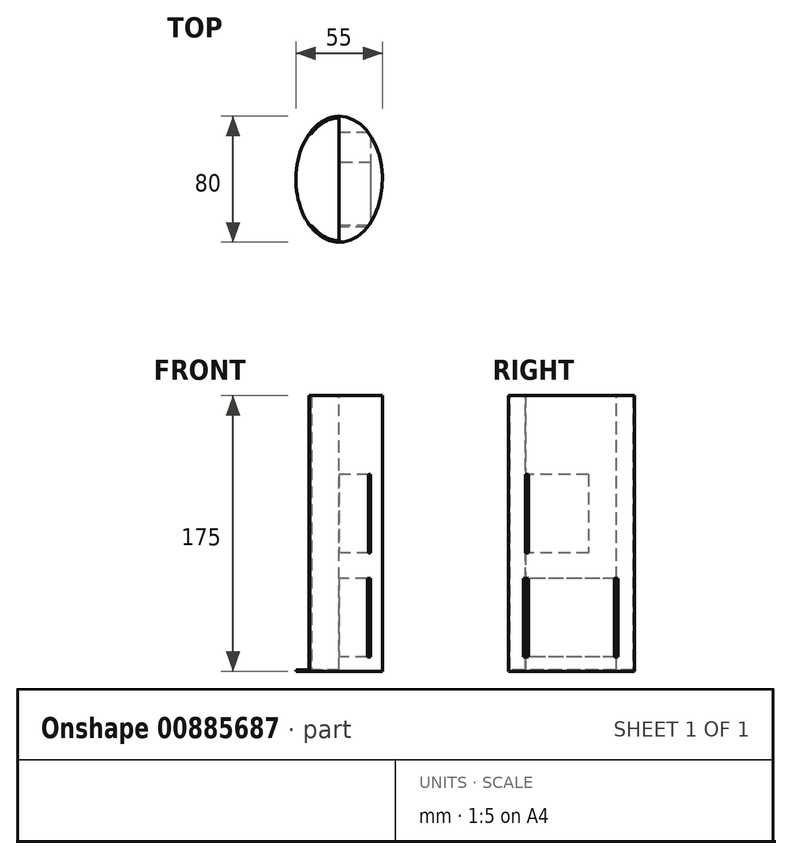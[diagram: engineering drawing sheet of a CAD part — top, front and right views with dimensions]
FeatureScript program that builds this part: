
annotation { "Feature Type Name" : "Feature", "Feature Type Description" : "" }
export const myFeature = defineFeature(function(context is Context, id is Id, definition is map)
    precondition{}
    {
        {
            var Q0;
            Q0=qCreatedBy(makeId("Top.planeOp"),FACE);
            var sketch = newSketch(context, id + "F0", { "sketchPlane" : qUnion([Q0])});
            skEllipse(sketch, "E0", {"center": v(-46.65, 29.27) * mm, "majorRadius": 27.5 * mm, "minorRadius": 40 * mm, "majorAxis": v(1, 0)});
            skSolve(sketch);
        }
        {
            var Q0;
            Q0 = qSketchRegion(id + "F0", true);
            extrude(context, id + "F1", {"entities" : qUnion([Q0]), "depth" : 175 * mm, "offsetDistance" : 25 * mm});
        }
        {
            var Q0;
            Q0=makeQuery(id+"F1.opExtrude","CAP_FACE",FACE,{"disambiguationData":[OSD([sQuery(id+"F0.wireOp",EDGE,"E0")])],"isStart":false});
            shell(context, id + "F2", {"entities" : qUnion([Q0]), "thickness" : 1 * mm});
        }
        {
            var Q0;
            Q0=makeQuery(id+"F1.opExtrude","CAP_FACE",FACE,{"disambiguationData":[OSD([sQuery(id+"F0.wireOp",EDGE,"E0")])],"isStart":false});
            var sketch = newSketch(context, id + "F3", { "sketchPlane" : qUnion([Q0])});
            skLineSegment(sketch, "E1.bottom", {"start": v(-60.73, 57.84) * mm, "end": v(-76, 57.84) * mm});
            skLineSegment(sketch, "E1.top", {"start": v(-60.73, 0) * mm, "end": v(-76, 0) * mm});
            skLineSegment(sketch, "E1.left", {"start": v(-60.73, 57.84) * mm, "end": v(-60.73, 0) * mm});
            skLineSegment(sketch, "E1.right", {"start": v(-76, 57.84) * mm, "end": v(-76, 0) * mm});
            skSolve(sketch);
        }
        {
            var Q0;
            {var subQ0=sQuery(id+"F3.wireOp",EDGE,"E1.bottom");var subQ1=sQuery(id+"F0.wireOp",EDGE,"E0");var subQ2=makeQuery(id+"F1.opExtrude","CAP_EDGE",EDGE,{"disambiguationData":[OSD([subQ1])],"isStart":false});var subQ3=makeQuery(id+"F3.imprint","INTERSECT",VERTEX,{"derivedFrom":[subQ2,subQ0]});Q0=makeQuery(id+"F3.imprint","IMPRINT",FACE,{"disambiguationData":[TD([[makeQuery(id+"F3.imprint","IMPRINT",EDGE,{"disambiguationData":[TD([[subQ3,-1.0]])],"derivedFrom":subQ2}),1.0]])]});}
            extrude(context, id + "F4", {"entities" : qUnion([Q0]), "operationType" : NewBodyOperationType.REMOVE, "oppositeDirection" : true, "depth" : 174 * mm, "offsetDistance" : 25 * mm});
        }
        {
            var Q0;
            {var subQ0=sQuery(id+"F0.wireOp",EDGE,"E0");Q0=makeQuery(id+"F4.boolean.opBoolean","MERGE",FACE,{"derivedFrom":[makeQuery(id+"F2.opShell","OFFSET_FACE",FACE,{"disambiguationData":[OSD([subQ0]),TDD([makeQuery(id+"F1.opExtrude","CAP_FACE",FACE,{"disambiguationData":[OSD([subQ0])],"isStart":true})])]})],"fromTools":[makeQuery(id+"F4.opExtrude","CAP_FACE",FACE,{"disambiguationData":[OSD([subQ0,sQuery(id+"F3.wireOp",EDGE,"idDmL1wW-uwLS-MqbP-2c12-nJMtcr108V6O.bottom"),sQuery(id+"F3.wireOp",EDGE,"idDmL1wW-uwLS-MqbP-2c12-nJMtcr108V6O.top")])],"isStart":false})]});}
            var sketch = newSketch(context, id + "F5", { "sketchPlane" : qUnion([Q0])});
            skPoint(sketch, "E2.oppositeSnap0", {"position": v(-46.65, -10.73) * mm});
            skLineSegment(sketch, "E2.bottom", {"start": v(-18.75, 71.84) * mm, "end": v(-46.65, 71.84) * mm});
            skLineSegment(sketch, "E2.top", {"start": v(-18.75, -16.12) * mm, "end": v(-46.65, -16.12) * mm});
            skLineSegment(sketch, "E2.left", {"start": v(-18.75, 71.84) * mm, "end": v(-18.75, -16.12) * mm});
            skLineSegment(sketch, "E2.right", {"start": v(-46.65, 71.84) * mm, "end": v(-46.65, -16.12) * mm});
            skSolve(sketch);
        }
        {
            var Q0;
            {var subQ0=sQuery(id+"F5.wireOp",EDGE,"p6g6H9hA-Dlka-ndgF-t6zo-Iuqqo2L0n8Ji.right");var subQ1=sQuery(id+"F0.wireOp",EDGE,"E0");var subQ2=makeQuery(id+"F2.opShell","OFFSET_EDGE",EDGE,{"disambiguationData":[OSD([subQ1]),TDD([makeQuery(id+"F1.opExtrude","CAP_EDGE",EDGE,{"disambiguationData":[OSD([subQ1])],"isStart":true})])]});var subQ3=makeQuery(id+"F5.imprint","INTERSECT",VERTEX,{"disambiguationData":[OD(0.0)],"derivedFrom":[subQ2,subQ0]});Q0=makeQuery(id+"F5.imprint","IMPRINT",FACE,{"disambiguationData":[TD([[makeQuery(id+"F5.imprint","IMPRINT",EDGE,{"disambiguationData":[TD([[subQ3,-1.0]])],"derivedFrom":subQ0}),1.0]])]});}
            var Q1;
            {var subQ0=sQuery(id+"F5.wireOp",EDGE,"E2.right");var subQ1=sQuery(id+"F0.wireOp",EDGE,"E0");var subQ2=makeQuery(id+"F2.opShell","OFFSET_EDGE",EDGE,{"disambiguationData":[OSD([subQ1]),TDD([makeQuery(id+"F1.opExtrude","CAP_EDGE",EDGE,{"disambiguationData":[OSD([subQ1])],"isStart":true})])]});var subQ3=makeQuery(id+"F5.imprint","INTERSECT",VERTEX,{"disambiguationData":[OD(0.0)],"derivedFrom":[subQ2,subQ0]});Q1=makeQuery(id+"F5.imprint","IMPRINT",FACE,{"disambiguationData":[TD([[makeQuery(id+"F5.imprint","IMPRINT",EDGE,{"disambiguationData":[TD([[subQ3,-1.0]])],"derivedFrom":subQ0}),1.0]])]});}
            extrude(context, id + "F6", {"entities" : qUnion([Q0, Q1]), "operationType" : NewBodyOperationType.ADD, "depth" : 174 * mm, "offsetDistance" : 25 * mm});
        }
        {
            var Q0;
            Q0=makeQuery(id+"F6.opExtrude","SWEPT_FACE",FACE,{"disambiguationData":[OSD([sQuery(id+"F5.wireOp",EDGE,"E2.right")])]});
            var sketch = newSketch(context, id + "F7", { "sketchPlane" : qUnion([Q0])});
            skLineSegment(sketch, "E3.bottom", {"start": v(-58.84, 59) * mm, "end": v(1.16, 59) * mm});
            skLineSegment(sketch, "E3.top", {"start": v(-58.84, 9) * mm, "end": v(1.16, 9) * mm});
            skLineSegment(sketch, "E3.left", {"start": v(-58.84, 59) * mm, "end": v(-58.84, 9) * mm});
            skLineSegment(sketch, "E3.right", {"start": v(1.16, 59) * mm, "end": v(1.16, 9) * mm});
            skLineSegment(sketch, "E4.bottom", {"start": v(-40, 125) * mm, "end": v(0, 125) * mm});
            skLineSegment(sketch, "E4.top", {"start": v(-40, 75) * mm, "end": v(0, 75) * mm});
            skLineSegment(sketch, "E4.left", {"start": v(-40, 125) * mm, "end": v(-40, 75) * mm});
            skLineSegment(sketch, "E4.right", {"start": v(0, 125) * mm, "end": v(0, 75) * mm});
            skSolve(sketch);
        }
        {
            var Q0;
            Q0 = qSketchRegion(id + "F7", true);
            extrude(context, id + "F8", {"entities" : qUnion([Q0]), "operationType" : NewBodyOperationType.REMOVE, "oppositeDirection" : true, "depth" : 20 * mm, "offsetDistance" : 25 * mm});
        }
    });
